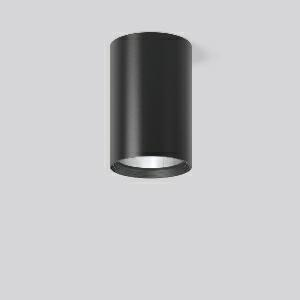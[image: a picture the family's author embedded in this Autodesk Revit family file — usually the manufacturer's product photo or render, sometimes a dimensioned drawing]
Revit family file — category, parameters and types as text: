
# Revit family: heledon_maxi_a_931218_003_3_76_690a
name_source: partatom
category: Lighting Fixtures
units: mm (PartAtom-declared; Revit-internal decimal feet)

## family parameters
Cut with Voids When Loaded = No
Host = Face
Light Source = No
Part Type = Normal
Room Calculation Point = No
Round Connector Dimension = Use Diameter
Shared = No

## types (1)
- HELEDON maxi A (1 x LED Modul 935, 3400 lm, 3500)
    Apparent Load = 25 VA
    Approval mark = CE
    CIE Flux Codes = 100 100 100 100 100
    Color Rendering = 92
    Color Temperature = 3500
    Default Elevation = 1800 mm
    Description = Series: HELEDON maxi
Cylindrical surface-mounted downlight. Housing: die-cast aluminium, powder-coated. Internal ceiling frame polycarbonate with bayonet mounting. Black plastic ring and recessed LED to prevent glare from the side. Optical assembly with reflector made of MIRO-Silver with 98% total light reflection for outstanding efficiency - can be changed without tools. Best colour rendering index Ra>90. Suitable for Ceiling mounting. Easy installation with a separate ceiling frame with bayonet mounting and plug connection. Driver integrated. Connected via plug-in connector. High quality converter without flickering and stroboscopic effect. The following accessories can be mounted without use of tools: interchangeable lenses, decorative glasses, honeycomb louvre, clear and frosted diffusers, white interchangeable plastic ring. 
Colour: deep black, matt (RAL 9005)
Diameter: 123 mm
Height: 183 mm
Lamp: LED
Socket: without socket
Colour temperature: 3500K
Colour rendering index (CRI): 92
System power: 25 W
Rated luminous flux: 3400 lm
Luminous efficiency: 136 lm/W
Control gear: Converter, dimmable, DALI
Protection class: I
Type of protection: IP 20
    Height = 183 mm
    Lamp = 1 x LED Modul 935
    Lamp Light Flux = 3400 lm
    Lamp count = 1
    Length = 123 mm
    Lifetime = 50000 h
    Luminous efficacy = 136 lm/W
    Manufacturer = RZB
    ModVariant = No
    Model = 931218.003.3.76
    Mounting Place = Ceiling
    Mounting Type = Surface mounted
    Number of Poles = 1
    OnlyDefault = Yes
    Power Factor = 1
    Product Name = HELEDON maxi A
    Product group = Surface mounted downlights
    ProductGroupID = 302
    Protection Class = Protection class I
    Protection Degree = IP 20
    RLX_Detail_Level = 1
    RLX_Emergency_Light_Flux = 0 lm
    RLX_Emergency_Type = 0
    RLX_Emergency_Type_DB = No
    RlxData = <blob elided: 99253 chars, md5=e66ba452>
    Socket = socket
    Standby Power = 0 W
    System Light Flux = 3400 lm
    System Power = 25 W
    Type Comments = Product without accessories
    Type Image = 931192.003.jpg
    URL = http://relux.com
    VarID = ---
    Voltage = 230 V
    Voltage Range = 220-240 V
    Weight = 0.00 kg
    Width = 0 mm  [stored 0 ft]

note: [stored X ft] marks values corroborated as IEEE doubles in the binary element streams (Revit-internal decimal feet)

## geometry (parser evidence)
native form markers: Blend x4, Sweep x11
no freeform markers — native parametric forms only
